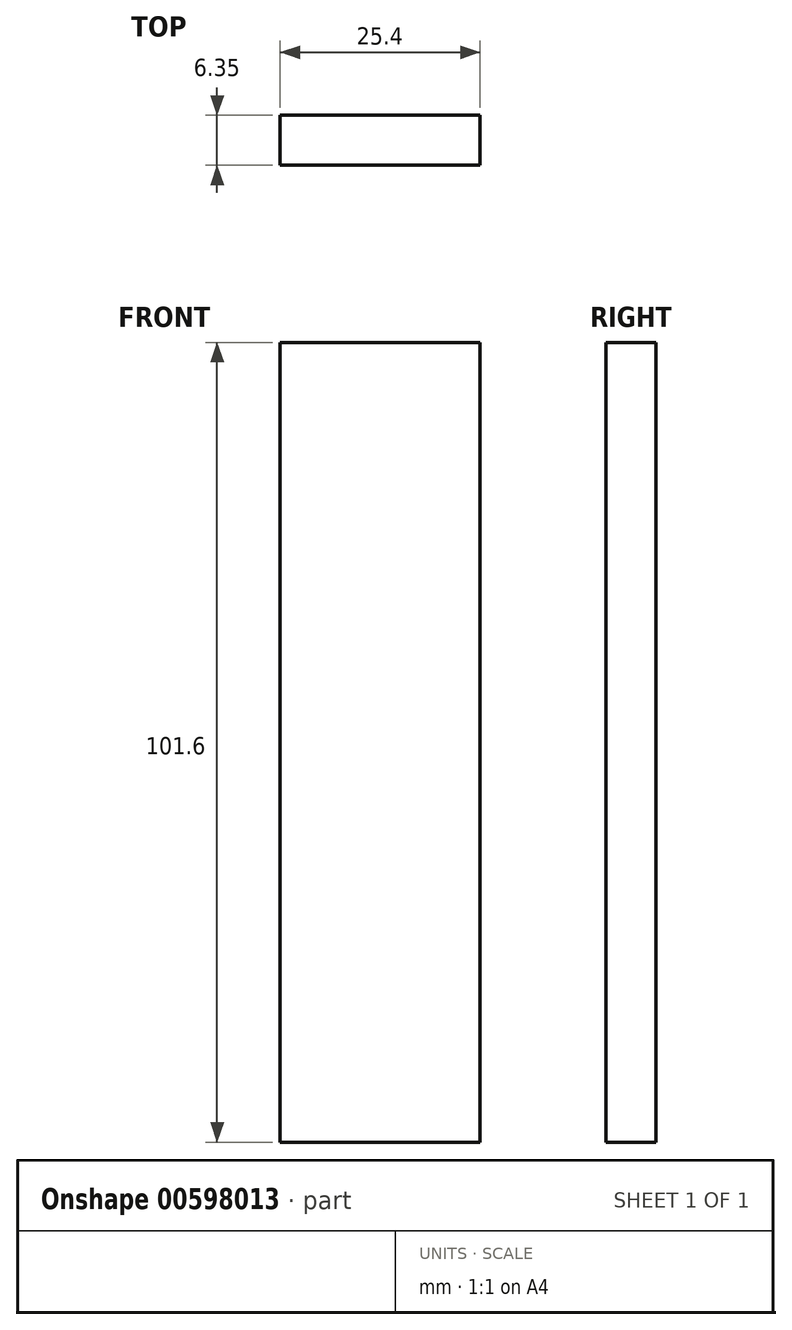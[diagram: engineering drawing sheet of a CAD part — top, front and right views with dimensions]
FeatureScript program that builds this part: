
annotation { "Feature Type Name" : "Feature", "Feature Type Description" : "" }
export const myFeature = defineFeature(function(context is Context, id is Id, definition is map)
    precondition{}
    {
        {
            var Q0;
            Q0=qCreatedBy(makeId("Front.planeOp"),FACE);
            var sketch = newSketch(context, id + "F0", { "sketchPlane" : qUnion([Q0])});
            skLineSegment(sketch, "E0.bottom", {"start": v(0, -457.2) * mm, "end": v(-762, -457.2) * mm});
            skLineSegment(sketch, "E0.top", {"start": v(0, 457.2) * mm, "end": v(-762, 457.2) * mm});
            skLineSegment(sketch, "E0.right", {"start": v(-762, -457.2) * mm, "end": v(-762, 457.2) * mm});
            skPoint(sketch, "E0.middle", {"position": v(0, 0) * mm});
            skLineSegment(sketch, "E1.bottom", {"start": v(-762, 457.2) * mm, "end": v(-736.6, 457.2) * mm});
            skLineSegment(sketch, "E1.top", {"start": v(-762, 355.6) * mm, "end": v(-736.6, 355.6) * mm});
            skLineSegment(sketch, "E1.left", {"start": v(-762, 457.2) * mm, "end": v(-762, 355.6) * mm});
            skLineSegment(sketch, "E1.right", {"start": v(-736.6, 457.2) * mm, "end": v(-736.6, 355.6) * mm});
            skLineSegment(sketch, "E2.0.1.0", {"start": v(-736.6, 254) * mm, "end": v(-736.6, 152.4) * mm});
            skLineSegment(sketch, "E2.0.1.1", {"start": v(-762, 254) * mm, "end": v(-736.6, 254) * mm});
            skLineSegment(sketch, "E2.0.1.2", {"start": v(-762, 254) * mm, "end": v(-762, 152.4) * mm});
            skLineSegment(sketch, "E2.0.1.3", {"start": v(-762, 152.4) * mm, "end": v(-736.6, 152.4) * mm});
            skLineSegment(sketch, "E2.0.2.0", {"start": v(-736.6, 50.8) * mm, "end": v(-736.6, -50.8) * mm});
            skLineSegment(sketch, "E2.0.2.1", {"start": v(-762, 50.8) * mm, "end": v(-736.6, 50.8) * mm});
            skLineSegment(sketch, "E2.0.2.2", {"start": v(-762, 50.8) * mm, "end": v(-762, -50.8) * mm});
            skLineSegment(sketch, "E2.0.2.3", {"start": v(-762, -50.8) * mm, "end": v(-736.6, -50.8) * mm});
            skLineSegment(sketch, "E2.0.3.0", {"start": v(-736.6, -152.4) * mm, "end": v(-736.6, -254) * mm});
            skLineSegment(sketch, "E2.0.3.1", {"start": v(-762, -152.4) * mm, "end": v(-736.6, -152.4) * mm});
            skLineSegment(sketch, "E2.0.3.2", {"start": v(-762, -152.4) * mm, "end": v(-762, -254) * mm});
            skLineSegment(sketch, "E2.0.3.3", {"start": v(-762, -254) * mm, "end": v(-736.6, -254) * mm});
            skLineSegment(sketch, "E2.0.4.0", {"start": v(-736.6, -355.6) * mm, "end": v(-736.6, -457.2) * mm});
            skLineSegment(sketch, "E2.0.4.1", {"start": v(-762, -355.6) * mm, "end": v(-736.6, -355.6) * mm});
            skLineSegment(sketch, "E2.0.4.2", {"start": v(-762, -355.6) * mm, "end": v(-762, -457.2) * mm});
            skLineSegment(sketch, "E2.0.4.3", {"start": v(-762, -457.2) * mm, "end": v(-736.6, -457.2) * mm});
            skLineSegment(sketch, "E2.direction1", {"start": v(-762, 355.6) * mm, "end": v(-736.6, 355.6) * mm, "construction": true});
            skLineSegment(sketch, "E2.direction2", {"start": v(-762, 355.6) * mm, "end": v(-762, 152.4) * mm, "construction": true});
            skLineSegment(sketch, "E3", {"start": v(0, 0) * mm, "end": v(0, 457.2) * mm, "construction": true});
            skLineSegment(sketch, "E4", {"start": v(0, 457.2) * mm, "end": v(0, -457.2) * mm, "construction": true});
            skPoint(sketch, "E0.left.end.orphan", {"position": v(762, 457.2) * mm});
            skPoint(sketch, "E5.orphan", {"position": v(762, -457.2) * mm});
            skLineSegment(sketch, "E6.MirrorCS", {"start": v(0, 457.2) * mm, "end": v(762, 457.2) * mm});
            skLineSegment(sketch, "E7.MirrorCS", {"start": v(762, 457.2) * mm, "end": v(762, 355.6) * mm});
            skLineSegment(sketch, "E8.MirrorCS", {"start": v(736.6, 457.2) * mm, "end": v(736.6, 355.6) * mm});
            skLineSegment(sketch, "E9.MirrorCS", {"start": v(762, 355.6) * mm, "end": v(762, 152.4) * mm, "construction": true});
            skLineSegment(sketch, "E10.MirrorCS", {"start": v(762, 254) * mm, "end": v(736.6, 254) * mm});
            skLineSegment(sketch, "E11.MirrorCS", {"start": v(736.6, 254) * mm, "end": v(736.6, 152.4) * mm});
            skLineSegment(sketch, "E12.MirrorCS", {"start": v(762, 152.4) * mm, "end": v(736.6, 152.4) * mm});
            skLineSegment(sketch, "E13.MirrorCS", {"start": v(762, -457.2) * mm, "end": v(762, 457.2) * mm});
            skLineSegment(sketch, "E14.MirrorCS", {"start": v(762, 50.8) * mm, "end": v(736.6, 50.8) * mm});
            skLineSegment(sketch, "E15.MirrorCS", {"start": v(736.6, 50.8) * mm, "end": v(736.6, -50.8) * mm});
            skLineSegment(sketch, "E16.MirrorCS", {"start": v(762, -50.8) * mm, "end": v(736.6, -50.8) * mm});
            skLineSegment(sketch, "E17.MirrorCS", {"start": v(762, -152.4) * mm, "end": v(736.6, -152.4) * mm});
            skLineSegment(sketch, "E18.MirrorCS", {"start": v(736.6, -152.4) * mm, "end": v(736.6, -254) * mm});
            skLineSegment(sketch, "E19.MirrorCS", {"start": v(762, -254) * mm, "end": v(736.6, -254) * mm});
            skLineSegment(sketch, "E20.MirrorCS", {"start": v(762, -152.4) * mm, "end": v(762, -254) * mm});
            skLineSegment(sketch, "E21.MirrorCS", {"start": v(762, -355.6) * mm, "end": v(736.6, -355.6) * mm});
            skLineSegment(sketch, "E22.MirrorCS", {"start": v(736.6, -355.6) * mm, "end": v(736.6, -457.2) * mm});
            skLineSegment(sketch, "E23.MirrorCS", {"start": v(762, -355.6) * mm, "end": v(762, -457.2) * mm});
            skLineSegment(sketch, "E24.MirrorCS", {"start": v(0, -457.2) * mm, "end": v(762, -457.2) * mm});
            skLineSegment(sketch, "E25", {"start": v(736.6, 355.6) * mm, "end": v(762, 355.6) * mm});
            skSolve(sketch);
        }
        {
            var Q0;
            {var subQ13=sQuery(id+"F0.wireOp",EDGE,"E0.bottom");Q0=makeQuery(id+"F0.imprint","IMPRINT",FACE,{"disambiguationData":[TD([[makeQuery(id+"F0.imprint","IMPRINT",EDGE,{"derivedFrom":subQ13}),-1.0]])]});}
            extrude(context, id + "F1", {"entities" : qUnion([Q0]), "depth" : 6.35 * mm, "offsetDistance" : 25.4 * mm});
        }
    });
